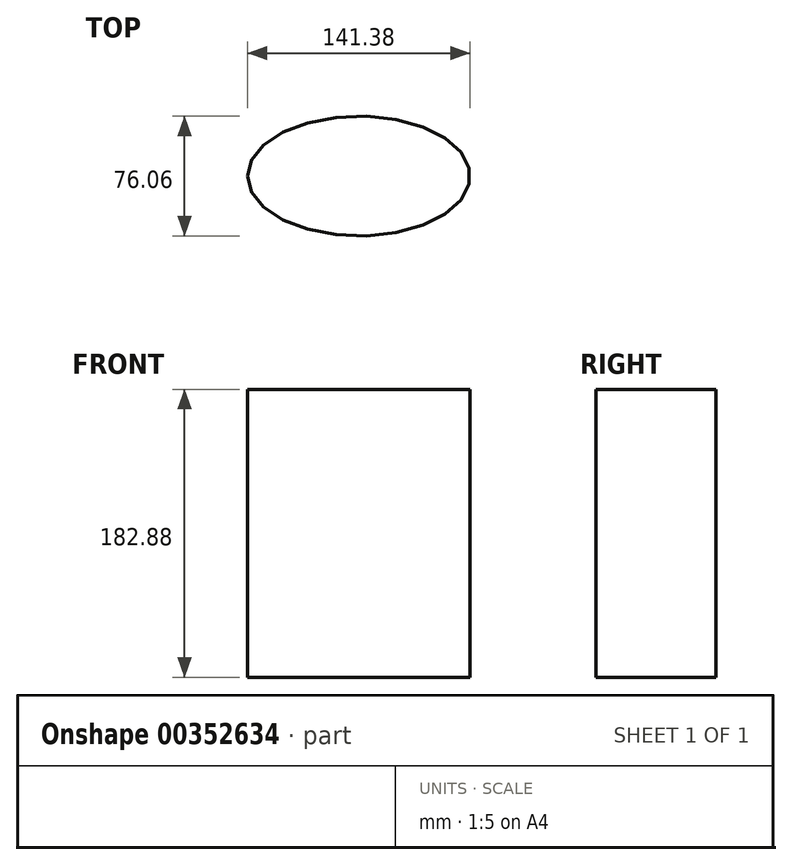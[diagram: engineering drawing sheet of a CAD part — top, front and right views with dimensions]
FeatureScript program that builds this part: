
annotation { "Feature Type Name" : "Feature", "Feature Type Description" : "" }
export const myFeature = defineFeature(function(context is Context, id is Id, definition is map)
    precondition{}
    {
        {
            var Q0;
            Q0=qCreatedBy(makeId("Top.planeOp"),FACE);
            var sketch = newSketch(context, id + "F0", { "sketchPlane" : qUnion([Q0])});
            skEllipse(sketch, "E0", {"center": v(0, 0) * mm, "majorRadius": 70.7 * mm, "minorRadius": 38.03 * mm, "majorAxis": v(-1, 0)});
            skSolve(sketch);
        }
        {
            var Q0;
            Q0 = qSketchRegion(id + "F0", true);
            extrude(context, id + "F1", {"entities" : qUnion([Q0]), "endBound" : BoundingType.SYMMETRIC, "depth" : 182.88 * mm});
        }
    });
